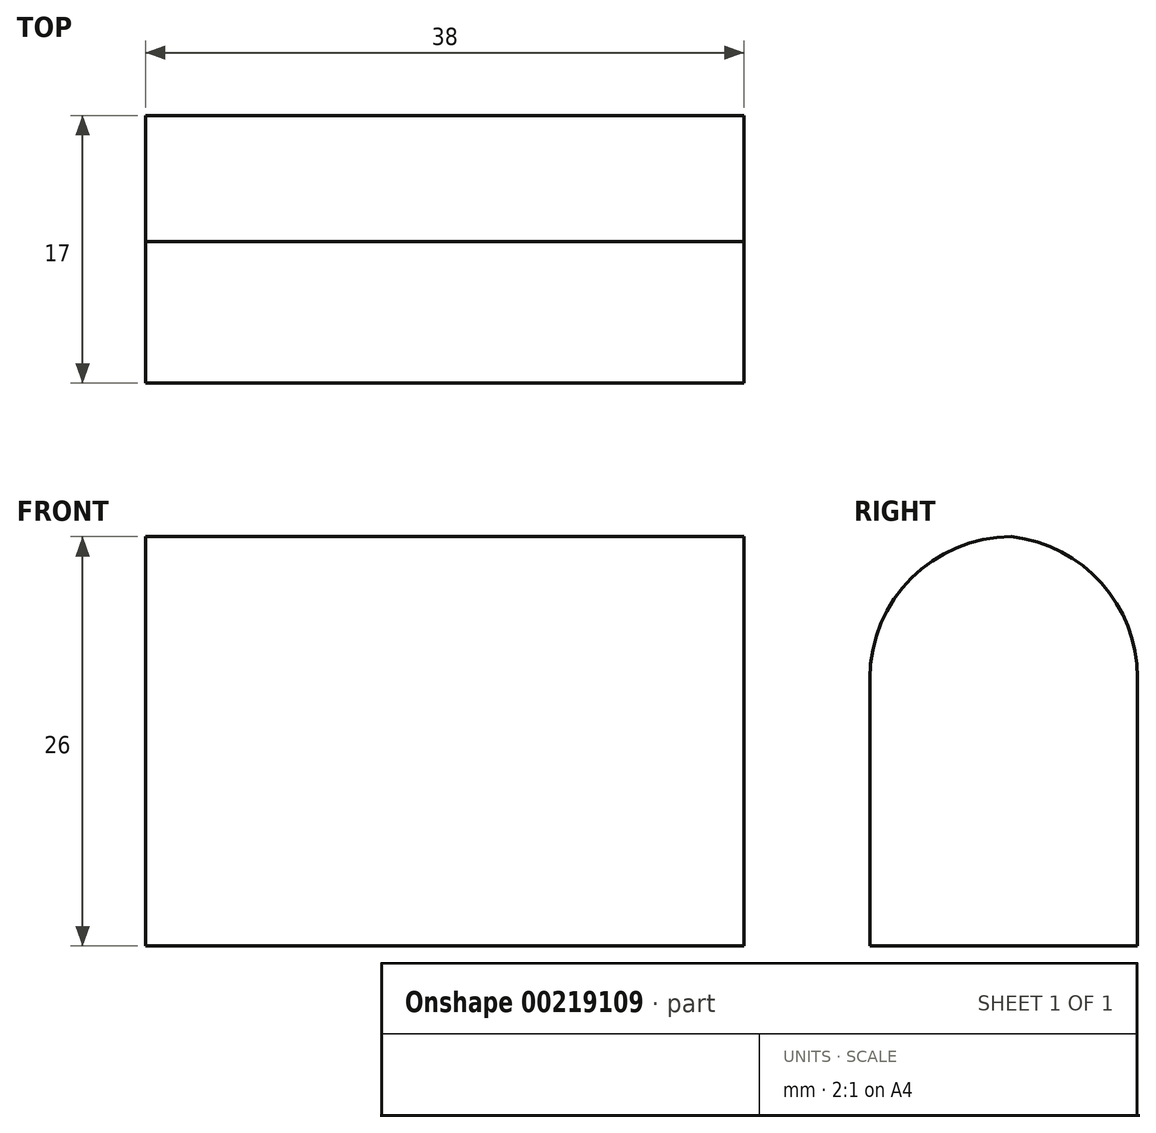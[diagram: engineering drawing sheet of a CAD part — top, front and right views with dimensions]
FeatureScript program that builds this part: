
annotation { "Feature Type Name" : "Feature", "Feature Type Description" : "" }
export const myFeature = defineFeature(function(context is Context, id is Id, definition is map)
    precondition{}
    {
        {
            var Q0;
            Q0=qCreatedBy(makeId("Front.planeOp"),FACE);
            var sketch = newSketch(context, id + "F0", { "sketchPlane" : qUnion([Q0])});
            skLineSegment(sketch, "E0.bottom", {"start": v(0, 0) * mm, "end": v(38, 0) * mm});
            skLineSegment(sketch, "E0.top", {"start": v(0, 26) * mm, "end": v(38, 26) * mm});
            skLineSegment(sketch, "E0.left", {"start": v(0, 0) * mm, "end": v(0, 26) * mm});
            skLineSegment(sketch, "E0.right", {"start": v(38, 0) * mm, "end": v(38, 26) * mm});
            skSolve(sketch);
        }
        {
            var Q0;
            Q0=makeQuery(id+"F0.imprint","IMPRINT",FACE,{"disambiguationData":[TD([[makeQuery(id+"F0.imprint","IMPRINT",EDGE,{"derivedFrom":sQuery(id+"F0.wireOp",EDGE,"E0.bottom")}),1.0]])]});
            extrude(context, id + "F1", {"entities" : qUnion([Q0]), "depth" : 17 * mm});
        }
        {
            var Q0;
            Q0=makeQuery(id+"F1.opExtrude","CAP_EDGE",EDGE,{"disambiguationData":[OSD([sQuery(id+"F0.wireOp",EDGE,"E0.top")])],"isStart":false});
            fillet(context, id + "F2", {"entities" : qUnion([Q0]), "radius" : 9 * mm, "tangentPropagation" : true, "allowEdgeOverflow" : false});
        }
        {
            var Q0;
            Q0=makeQuery(id+"F1.opExtrude","CAP_EDGE",EDGE,{"disambiguationData":[OSD([sQuery(id+"F0.wireOp",EDGE,"E0.top")])],"isStart":true});
            fillet(context, id + "F3", {"entities" : qUnion([Q0]), "radius" : 9 * mm, "tangentPropagation" : true, "allowEdgeOverflow" : false});
        }
    });
